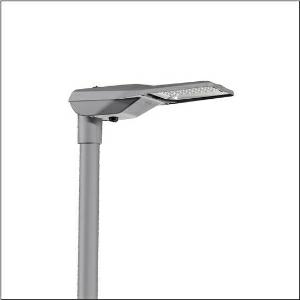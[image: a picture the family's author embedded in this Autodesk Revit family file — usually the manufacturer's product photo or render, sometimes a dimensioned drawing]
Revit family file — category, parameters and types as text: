
# Revit family: streetlight_sl_21_mini___p0_5a_5xe2v33t08jb_709b
name_source: partatom
category: Lighting Fixtures
units: mm (PartAtom-declared; Revit-internal decimal feet)

## family parameters
Cut with Voids When Loaded = No
Host = Face
Light Source = No
Part Type = Normal
Room Calculation Point = No
Round Connector Dimension = Use Diameter
Shared = No

## types (1)
- --- (1 x LED, 12720 lm, 88.6 W, 3000K)
    Apparent Load = 89 VA
    CIE Flux Codes = 37 73 96 100 100
    Color Rendering = 70
    Color Temperature = 3000K
    Default Elevation = 1800 mm
    Description = Streetlight SL 21 mini, mast luminaire, primary light control with lens, of PMMA, primary optical cover: cover, of toughened safety glass, transparent, light distribution: P0.5a, light emission: direct distribution, primary light characteristic: asymmetric, installation type: post-top, side-entry, LED, High Power LED, rated luminous flux: 12.720lm, luminous efficacy: 144lm/W, light colour: 730, colour temperature: 3000K, control gear: D4i, control: pre-setting: logarithmic dimming characteristic, flexible luminous flux parameterisation, time-dependent luminous flux control, constant luminous flux control, overheat protection, mains connection: 220..240V, AC, 50/60Hz, start of lifetime: 89W, end of service life: 92W, reduction: 41W, luminaire housing, of diecast aluminium, powder-coated, Siteco® metallic grey (DB 702S), corrosivity category C5 mid according to DIN EN ISO 12944, multi-level sealing system, sealing non-destructively replaceable, inclination adjustable: 0°, 5°, 10°, 15°, please order mast flange separately, length: 628mm, width: 235mm, height: 110mm, mast flange for spigot size: 42mm (side-entry): 5XC10008XM4, 60/48mm (side-entry/post-top): 5XC10108XM2, 76/60mm (side-entry/post-top): 5XC10108XM1, mounting height: 4..8m, Smart Interface below and above, protection rating (complete): IP66, insulation class (complete): insulation class II (safety insulation), certification: CE, ENEC, ENEC+, VDE, impact resistance: IK09, permissible operating ambient temperature for outdoor applications: -40..+50°C, standard-compliant lighting for roads and squares, packaging unit: 1 piece

Light Distribution: P0.5a
    Height = 110 mm
    Lamp = 1 x LED
    Lamp Light Flux = 12720 lm
    Lamp Power = 88.6 W
    Lamp count = 1
    Length = 625 mm
    Luminous efficacy = 144 lm/W
    Manufacturer = Siteco
    ModVariant = No
    Model = 5XE2V33T08JB
    Number of Poles = 1
    OnlyDefault = Yes
    Power Factor = 1
    Product Name = Streetlight SL 21 mini | P0.5a
    Product group = mast luminaire | pylon top
    ProductGroupID = 6100
    Protection Class = Protection class II
    Protection Degree = IP 66
    RLX_Detail_Level = 1
    RLX_Emergency_Light_Flux = 0 lm
    RLX_Emergency_Type = 0
    RLX_Emergency_Type_DB = No
    RlxData = <blob elided: 26109 chars, md5=1119ee23>
    Socket = socket
    Standby Power = 0 W
    System Light Flux = 12720 lm
    System Power = 89 W
    Type Comments = factory setting: luminous flux: 100 % | dim-lin: 254 | 915 mA
    Type Image = l_1003514.jpg
    URL = http://relux.com
    VarID = @adj_009621
    Voltage = 0 V
    Weight = 0.00 kg
    Width = 234 mm

## geometry (parser evidence)
native form markers: Blend x4, Sweep x12
no freeform markers — native parametric forms only
